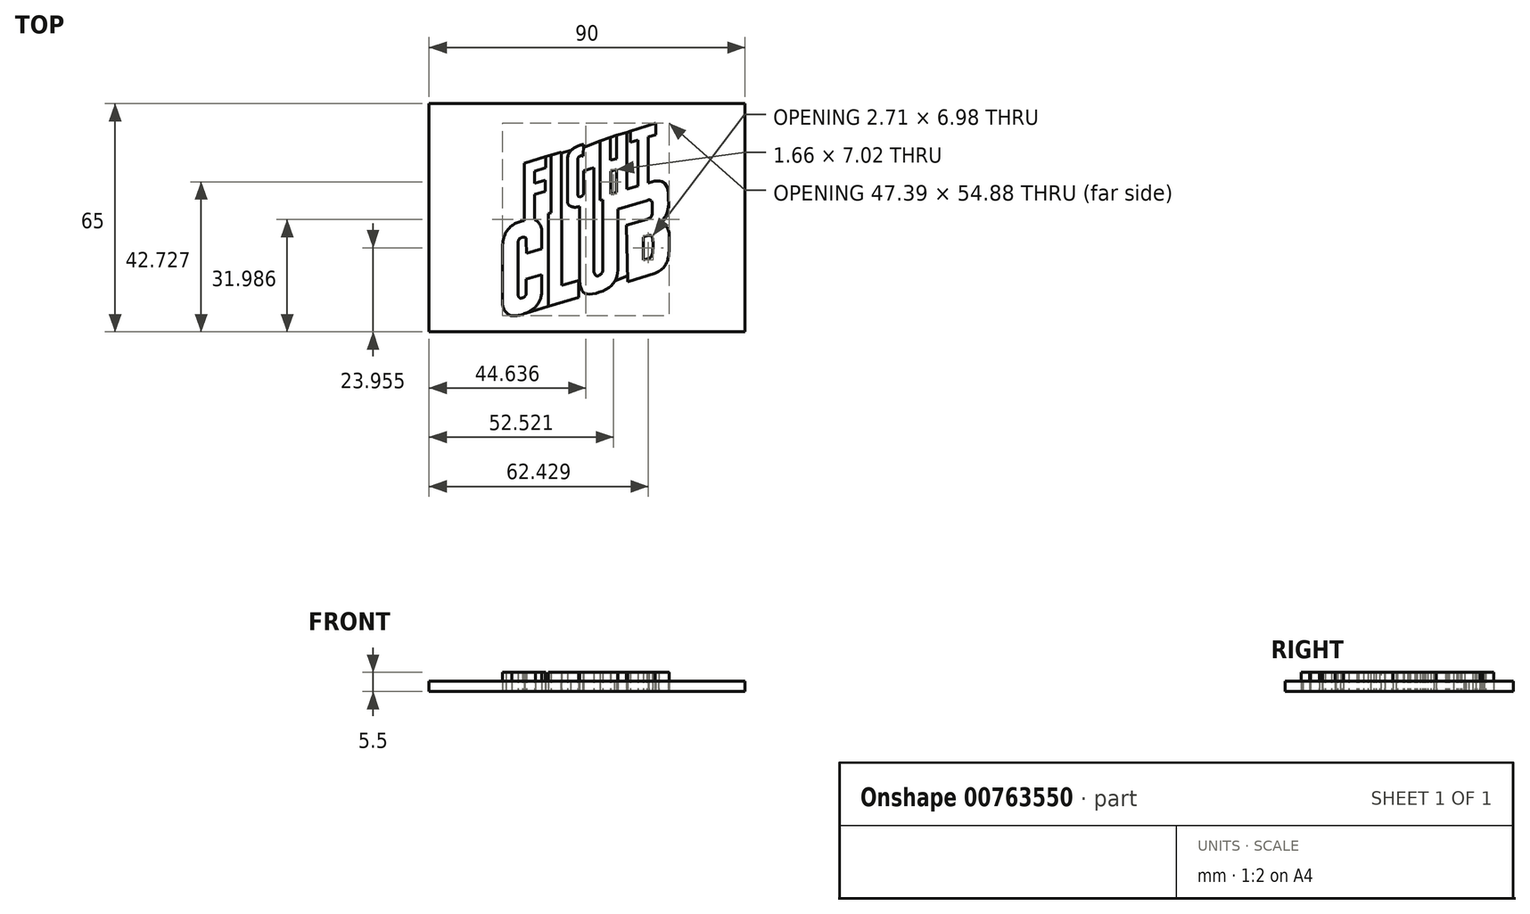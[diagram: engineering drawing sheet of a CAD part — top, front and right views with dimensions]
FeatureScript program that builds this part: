
annotation { "Feature Type Name" : "Feature", "Feature Type Description" : "" }
export const myFeature = defineFeature(function(context is Context, id is Id, definition is map)
    precondition{}
    {
        {
            var Q0;
            Q0=qCreatedBy(makeId("Top.planeOp"),FACE);
            var sketch = newSketch(context, id + "F0", { "sketchPlane" : qUnion([Q0])});
            skLineSegment(sketch, "E0", {"start": v(0, 29.17) * mm, "end": v(0, 40.63) * mm, "construction": true});
            skLineSegment(sketch, "E1", {"start": v(-11.79, 14.3) * mm, "end": v(-11.79, 17.39) * mm});
            skLineSegment(sketch, "E2", {"start": v(-11.79, 17.39) * mm, "end": v(-17.9, 15.52) * mm});
            skLineSegment(sketch, "E3", {"start": v(-17.9, 15.52) * mm, "end": v(-17.9, -0.84) * mm});
            skArc(sketch, "E4", {"start": v(-17.9, -0.84) * mm, "mid": v(-20.86, -1.84) * mm, "end": v(-23.05, -4.06) * mm});
            skArc(sketch, "E5", {"start": v(-23.05, -4.06) * mm, "mid": v(-23.84, -6) * mm, "end": v(-24.06, -8.1) * mm});
            skLineSegment(sketch, "E6", {"start": v(-24.06, -8.1) * mm, "end": v(-24.06, -24.5) * mm});
            skArc(sketch, "E7", {"start": v(-24.06, -24.5) * mm, "mid": v(-23.32, -26.69) * mm, "end": v(-21.4, -27.95) * mm});
            skArc(sketch, "E8", {"start": v(-21.4, -27.95) * mm, "mid": v(-17.85, -27.32) * mm, "end": v(-14.77, -25.45) * mm});
            skArc(sketch, "E9", {"start": v(-14.77, -25.45) * mm, "mid": v(-13.44, -23.46) * mm, "end": v(-12.97, -21.1) * mm});
            skLineSegment(sketch, "E10", {"start": v(-12.97, -21.1) * mm, "end": v(-12.9, -16.21) * mm});
            skLineSegment(sketch, "E11", {"start": v(-12.9, -16.21) * mm, "end": v(-17.32, -17.51) * mm});
            skLineSegment(sketch, "E12", {"start": v(-17.32, -17.51) * mm, "end": v(-17.32, -21.33) * mm});
            skArc(sketch, "E13", {"start": v(-18.38, -22.81) * mm, "mid": v(-17.61, -22.24) * mm, "end": v(-17.32, -21.33) * mm});
            skFitSpline(sketch, "E14", {"points": [v(-18.38, -22.81) * mm, v(-19.26, -22.81) * mm, v(-19.6, -22.2) * mm, v(-19.65, -21.74) * mm], "startDerivative": vector(-2.6, -0.52) * mm, "endDerivative": vector(-0.03, 1.52) * mm});
            skLineSegment(sketch, "E15", {"start": v(-19.65, -21.74) * mm, "end": v(-19.65, -7.2) * mm});
            skFitSpline(sketch, "E16", {"points": [v(-19.65, -7.2) * mm, v(-19.34, -6.08) * mm, v(-18.64, -5.6) * mm, v(-17.55, -5.65) * mm, v(-17.32, -6.58) * mm], "startDerivative": vector(0.18, 5.85) * mm, "endDerivative": vector(0, -4.67) * mm});
            skLineSegment(sketch, "E17", {"start": v(-17.32, -6.58) * mm, "end": v(-17.27, -10.17) * mm});
            skLineSegment(sketch, "E18", {"start": v(-17.27, -10.17) * mm, "end": v(-12.9, -8.8) * mm});
            skLineSegment(sketch, "E19", {"start": v(-12.9, -8.8) * mm, "end": v(-12.9, -4.15) * mm});
            skFitSpline(sketch, "E20", {"points": [v(-12.9, -4.15) * mm, v(-13.23, -2.36) * mm, v(-14.26, -0.9) * mm, v(-14.84, -0.62) * mm], "startDerivative": vector(-0.1, 5.35) * mm, "endDerivative": vector(-2.4, 0.79) * mm});
            skLineSegment(sketch, "E21", {"start": v(-14.84, -0.62) * mm, "end": v(-14.91, -0.62) * mm});
            skLineSegment(sketch, "E22", {"start": v(-14.91, -0.62) * mm, "end": v(-14.91, 6.66) * mm});
            skLineSegment(sketch, "E23", {"start": v(-14.91, 6.66) * mm, "end": v(-11.93, 7.57) * mm});
            skLineSegment(sketch, "E24", {"start": v(-11.93, 7.57) * mm, "end": v(-11.93, 10.68) * mm});
            skLineSegment(sketch, "E25", {"start": v(-11.93, 10.68) * mm, "end": v(-14.84, 9.85) * mm});
            skLineSegment(sketch, "E26", {"start": v(-14.84, 9.85) * mm, "end": v(-14.91, 9.82) * mm});
            skLineSegment(sketch, "E27", {"start": v(-14.91, 9.82) * mm, "end": v(-14.91, 13.28) * mm});
            skLineSegment(sketch, "E28", {"start": v(-14.91, 13.28) * mm, "end": v(-11.79, 14.3) * mm});
            skLineSegment(sketch, "E29", {"start": v(-7.35, 18.73) * mm, "end": v(-10.24, 17.82) * mm});
            skLineSegment(sketch, "E30", {"start": v(-10.24, 17.82) * mm, "end": v(-10.24, 1.4) * mm});
            skLineSegment(sketch, "E31", {"start": v(-10.24, 1.4) * mm, "end": v(-10.98, 1.14) * mm});
            skLineSegment(sketch, "E32", {"start": v(-10.98, 1.14) * mm, "end": v(-10.98, -25.2) * mm});
            skLineSegment(sketch, "E33", {"start": v(-10.98, -25.2) * mm, "end": v(-2.44, -22.65) * mm});
            skLineSegment(sketch, "E34", {"start": v(-2.44, -22.65) * mm, "end": v(-2.44, -17.83) * mm});
            skLineSegment(sketch, "E35", {"start": v(-2.44, -17.83) * mm, "end": v(-7.2, -19.25) * mm});
            skLineSegment(sketch, "E36", {"start": v(-7.2, -19.25) * mm, "end": v(-7.35, 18.73) * mm});
            skFitSpline(sketch, "E37", {"points": [v(-1.02, 20.93) * mm, v(-3.27, 20.17) * mm, v(-4.95, 18.7) * mm, v(-5.6, 16.65) * mm], "startDerivative": vector(-6.79, -1.77) * mm, "endDerivative": vector(-0.44, -7.25) * mm});
            skLineSegment(sketch, "E38", {"start": v(-5.6, 16.65) * mm, "end": v(-5.6, 4.51) * mm});
            skFitSpline(sketch, "E39", {"points": [v(-5.6, 4.51) * mm, v(-4.75, 3.3) * mm, v(-3.3, 3.02) * mm, v(-2.22, 3.16) * mm], "startDerivative": vector(0.44, -4.8) * mm, "endDerivative": vector(3.34, 0.64) * mm});
            skLineSegment(sketch, "E40", {"start": v(-2.22, 3.16) * mm, "end": v(-2.13, 3.16) * mm});
            skLineSegment(sketch, "E41", {"start": v(-2.13, 3.16) * mm, "end": v(-2.13, -18.02) * mm});
            skFitSpline(sketch, "E42", {"points": [v(-2.13, -18.02) * mm, v(-1.81, -19.83) * mm, v(-1.42, -20.7) * mm, v(-0.72, -21.43) * mm, v(0.48, -21.75) * mm, v(3.1, -21.35) * mm, v(5.96, -20.08) * mm, v(7.58, -18.53) * mm, v(8.4, -16.8) * mm, v(8.78, -14.72) * mm, v(8.81, -13.7) * mm], "startDerivative": vector(0.88, -18.82) * mm, "endDerivative": vector(0, 11.89) * mm});
            skLineSegment(sketch, "E43", {"start": v(8.81, -13.7) * mm, "end": v(8.81, 2.4) * mm});
            skLineSegment(sketch, "E44", {"start": v(8.81, 2.4) * mm, "end": v(17.06, 4.93) * mm});
            skFitSpline(sketch, "E45", {"points": [v(17.06, 4.93) * mm, v(17.61, 5.1) * mm, v(18.2, 4.93) * mm, v(18.53, 4.12) * mm, v(18.58, 3.23) * mm, v(18.52, 1.11) * mm, v(18.22, 0.23) * mm, v(17.68, -0.18) * mm, v(17.06, -0.42) * mm], "startDerivative": vector(5.26, 2.17) * mm, "endDerivative": vector(-5.78, -1.92) * mm});
            skLineSegment(sketch, "E46", {"start": v(17.06, -0.42) * mm, "end": v(11.24, -2.1) * mm});
            skLineSegment(sketch, "E47", {"start": v(11.24, -2.1) * mm, "end": v(11.52, -18.24) * mm});
            skLineSegment(sketch, "E48", {"start": v(11.52, -18.24) * mm, "end": v(19.26, -15.85) * mm});
            skFitSpline(sketch, "E49", {"points": [v(19.26, -15.85) * mm, v(20.2, -15.4) * mm, v(21.74, -14.25) * mm, v(22.83, -12.4) * mm, v(23.27, -10.48) * mm, v(23.33, -8.15) * mm], "startDerivative": vector(5.89, 2.48) * mm, "endDerivative": vector(0.02, 10.66) * mm});
            skFitSpline(sketch, "E50", {"points": [v(23.33, -8.15) * mm, v(23.33, -6.25) * mm, v(23.33, -5.01) * mm, v(23.33, -4.99) * mm, v(23.33, -4.12) * mm, v(22.64, -2.52) * mm, v(21.3, -1.73) * mm, v(20.42, -1.7) * mm, v(21.09, -1.18) * mm, v(21.98, -0.25) * mm, v(23.04, 2.14) * mm, v(23.2, 3.97) * mm, v(23.17, 6.68) * mm, v(23.13, 7.4) * mm, v(22.61, 9.27) * mm, v(21.4, 10.32) * mm, v(19.66, 10.5) * mm, v(17.56, 9.93) * mm], "startDerivative": vector(-0.03, 29.07) * mm, "endDerivative": vector(-29.21, -9.9) * mm});
            skLineSegment(sketch, "E51", {"start": v(17.56, 9.93) * mm, "end": v(17.44, 9.93) * mm});
            skLineSegment(sketch, "E52", {"start": v(17.44, 9.93) * mm, "end": v(17.44, 23.05) * mm});
            skLineSegment(sketch, "E53", {"start": v(17.44, 23.05) * mm, "end": v(19.62, 23.72) * mm});
            skLineSegment(sketch, "E54", {"start": v(19.62, 23.72) * mm, "end": v(19.62, 26.93) * mm});
            skLineSegment(sketch, "E55", {"start": v(19.62, 26.93) * mm, "end": v(12.3, 24.63) * mm});
            skLineSegment(sketch, "E56", {"start": v(12.3, 24.63) * mm, "end": v(12.3, 21.56) * mm});
            skLineSegment(sketch, "E57", {"start": v(12.3, 21.56) * mm, "end": v(14.5, 22.17) * mm});
            skLineSegment(sketch, "E58", {"start": v(14.5, 22.17) * mm, "end": v(14.5, 9.05) * mm});
            skLineSegment(sketch, "E59", {"start": v(14.5, 9.05) * mm, "end": v(11.35, 8.14) * mm});
            skLineSegment(sketch, "E60", {"start": v(11.35, 8.14) * mm, "end": v(11.35, 24.33) * mm});
            skLineSegment(sketch, "E61", {"start": v(11.35, 24.33) * mm, "end": v(8.42, 23.49) * mm});
            skLineSegment(sketch, "E62", {"start": v(8.42, 23.49) * mm, "end": v(8.42, 16.84) * mm});
            skLineSegment(sketch, "E63", {"start": v(8.42, 16.84) * mm, "end": v(6.67, 16.37) * mm});
            skLineSegment(sketch, "E64", {"start": v(6.67, 16.37) * mm, "end": v(6.67, 22.88) * mm});
            skLineSegment(sketch, "E65", {"start": v(6.67, 22.88) * mm, "end": v(3.73, 21.86) * mm});
            skLineSegment(sketch, "E66", {"start": v(3.73, 21.86) * mm, "end": v(3.73, 4.97) * mm});
            skLineSegment(sketch, "E67", {"start": v(3.73, 4.97) * mm, "end": v(4.46, 5.13) * mm});
            skLineSegment(sketch, "E68", {"start": v(4.46, 5.13) * mm, "end": v(4.46, -14.27) * mm});
            skFitSpline(sketch, "E69", {"points": [v(4.46, -14.27) * mm, v(4.46, -15.18) * mm, v(3.72, -16.26) * mm, v(2.72, -16.55) * mm, v(2.06, -15.8) * mm, v(1.94, -14.27) * mm], "startDerivative": vector(0, -3.25) * mm, "endDerivative": vector(-0.37, 7.2) * mm});
            skLineSegment(sketch, "E70", {"start": v(1.94, -14.27) * mm, "end": v(1.94, 14.26) * mm});
            skLineSegment(sketch, "E71", {"start": v(1.94, 14.26) * mm, "end": v(-0.98, 13.41) * mm});
            skPoint(sketch, "E71.endSnap0", {"position": v(3.73, 13.41) * mm});
            skLineSegment(sketch, "E72", {"start": v(-0.98, 13.41) * mm, "end": v(-0.98, 7.4) * mm});
            skFitSpline(sketch, "E73", {"points": [v(-0.98, 7.4) * mm, v(-0.98, 7.13) * mm, v(-1.1, 6.59) * mm, v(-1.46, 6.16) * mm, v(-2.38, 6) * mm, v(-2.65, 6.68) * mm], "startDerivative": vector(-0.05, -1.86) * mm, "endDerivative": vector(0.17, 3.62) * mm});
            skLineSegment(sketch, "E74", {"start": v(-2.65, 6.68) * mm, "end": v(-2.65, 16.65) * mm});
            skArc(sketch, "E75", {"start": v(-1.57, 17.66) * mm, "mid": v(-2.33, 17.39) * mm, "end": v(-2.65, 16.65) * mm});
            skArc(sketch, "E76", {"start": v(-1.18, 17.52) * mm, "mid": v(-1.37, 17.62) * mm, "end": v(-1.57, 17.66) * mm});
            skLineSegment(sketch, "E77", {"start": v(-1.18, 17.52) * mm, "end": v(-1.02, 20.93) * mm});
            skLineSegment(sketch, "E78", {"start": v(6.69, 13.22) * mm, "end": v(6.69, 6.72) * mm});
            skLineSegment(sketch, "E79", {"start": v(6.69, 6.72) * mm, "end": v(8.35, 7.26) * mm});
            skLineSegment(sketch, "E80", {"start": v(8.35, 7.26) * mm, "end": v(8.35, 13.74) * mm});
            skLineSegment(sketch, "E81", {"start": v(8.35, 13.74) * mm, "end": v(6.69, 13.22) * mm});
            skLineSegment(sketch, "E82", {"start": v(16.08, -5.5) * mm, "end": v(16.08, -12.04) * mm});
            skLineSegment(sketch, "E83", {"start": v(16.08, -12.04) * mm, "end": v(17.68, -11.53) * mm});
            skFitSpline(sketch, "E84", {"points": [v(17.68, -11.53) * mm, v(18.26, -11.11) * mm, v(18.66, -9.8) * mm, v(18.78, -7.26) * mm, v(18.46, -5.26) * mm, v(17.88, -5) * mm, v(16.08, -5.5) * mm], "startDerivative": vector(5.42, 2.74) * mm, "endDerivative": vector(-10.7, -3.8) * mm});
            skPoint(sketch, "E85.middle", {"position": v(0, 0) * mm});
            skPoint(sketch, "E86.start.orphan", {"position": v(-26.8, 29.76) * mm});
            skPoint(sketch, "E87.start.orphan", {"position": v(26.8, 29.76) * mm});
            skPoint(sketch, "E88.top.end.orphan", {"position": v(-26.8, -29.76) * mm});
            skPoint(sketch, "E88.top.start.orphan", {"position": v(26.8, -29.76) * mm});
            skPoint(sketch, "E89.bottom.start.orphan", {"position": v(-23.32, -26.69) * mm});
            skLineSegment(sketch, "E90.bottom", {"start": v(45, 32.5) * mm, "end": v(-45, 32.5) * mm});
            skLineSegment(sketch, "E90.top", {"start": v(45, -32.5) * mm, "end": v(-45, -32.5) * mm});
            skLineSegment(sketch, "E90.left", {"start": v(45, 32.5) * mm, "end": v(45, -32.5) * mm});
            skLineSegment(sketch, "E90.right", {"start": v(-45, 32.5) * mm, "end": v(-45, -32.5) * mm});
            skSolve(sketch);
        }
        {
            var Q0;
            Q0=makeQuery(id+"F0.imprint","IMPRINT",FACE,{"disambiguationData":[TD([[makeQuery(id+"F0.imprint","IMPRINT",EDGE,{"derivedFrom":sQuery(id+"F0.wireOp",EDGE,"E1")}),-1.0]])]});
            extrude(context, id + "F1", {"entities" : qUnion([Q0]), "depth" : 3 * mm, "offsetDistance" : 25 * mm});
        }
        {
            var Q0;
            Q0=makeQuery(id+"F0.imprint","IMPRINT",FACE,{"disambiguationData":[TD([[makeQuery(id+"F0.imprint","IMPRINT",EDGE,{"derivedFrom":sQuery(id+"F0.wireOp",EDGE,"E1")}),1.0]])]});
            var Q1;
            Q1=makeQuery(id+"F0.imprint","IMPRINT",FACE,{"disambiguationData":[TD([[makeQuery(id+"F0.imprint","IMPRINT",EDGE,{"derivedFrom":sQuery(id+"F0.wireOp",EDGE,"E29")}),1.0]])]});
            var Q2;
            Q2=makeQuery(id+"F0.imprint","IMPRINT",FACE,{"disambiguationData":[TD([[makeQuery(id+"F0.imprint","IMPRINT",EDGE,{"derivedFrom":sQuery(id+"F0.wireOp",EDGE,"E37")}),1.0]])]});
            extrude(context, id + "F2", {"entities" : qUnion([Q0, Q1, Q2]), "depth" : 5.5 * mm, "offsetDistance" : 25 * mm});
        }
        {
            var Q0;
            Q0=makeQuery(id+"F1.opExtrude","CAP_FACE",FACE,{"disambiguationData":[OSD([sQuery(id+"F0.wireOp",EDGE,"E1"),sQuery(id+"F0.wireOp",EDGE,"E2"),sQuery(id+"F0.wireOp",EDGE,"E3"),sQuery(id+"F0.wireOp",EDGE,"E4"),sQuery(id+"F0.wireOp",EDGE,"E5"),sQuery(id+"F0.wireOp",EDGE,"E6"),sQuery(id+"F0.wireOp",EDGE,"E7"),sQuery(id+"F0.wireOp",EDGE,"E8"),sQuery(id+"F0.wireOp",EDGE,"E9"),sQuery(id+"F0.wireOp",EDGE,"E10"),sQuery(id+"F0.wireOp",EDGE,"E11"),sQuery(id+"F0.wireOp",EDGE,"E12"),sQuery(id+"F0.wireOp",EDGE,"E13"),sQuery(id+"F0.wireOp",EDGE,"E14"),sQuery(id+"F0.wireOp",EDGE,"E15"),sQuery(id+"F0.wireOp",EDGE,"E16"),sQuery(id+"F0.wireOp",EDGE,"E17"),sQuery(id+"F0.wireOp",EDGE,"E18"),sQuery(id+"F0.wireOp",EDGE,"E19"),sQuery(id+"F0.wireOp",EDGE,"E20"),sQuery(id+"F0.wireOp",EDGE,"E21"),sQuery(id+"F0.wireOp",EDGE,"E22"),sQuery(id+"F0.wireOp",EDGE,"E23"),sQuery(id+"F0.wireOp",EDGE,"E24"),sQuery(id+"F0.wireOp",EDGE,"E25"),sQuery(id+"F0.wireOp",EDGE,"E26"),sQuery(id+"F0.wireOp",EDGE,"E27"),sQuery(id+"F0.wireOp",EDGE,"E28"),sQuery(id+"F0.wireOp",EDGE,"E29"),sQuery(id+"F0.wireOp",EDGE,"E30"),sQuery(id+"F0.wireOp",EDGE,"E31"),sQuery(id+"F0.wireOp",EDGE,"E32"),sQuery(id+"F0.wireOp",EDGE,"E33"),sQuery(id+"F0.wireOp",EDGE,"E34"),sQuery(id+"F0.wireOp",EDGE,"E35"),sQuery(id+"F0.wireOp",EDGE,"E36"),sQuery(id+"F0.wireOp",EDGE,"E37"),sQuery(id+"F0.wireOp",EDGE,"E38"),sQuery(id+"F0.wireOp",EDGE,"E39"),sQuery(id+"F0.wireOp",EDGE,"E40"),sQuery(id+"F0.wireOp",EDGE,"E41"),sQuery(id+"F0.wireOp",EDGE,"E42"),sQuery(id+"F0.wireOp",EDGE,"E43"),sQuery(id+"F0.wireOp",EDGE,"E44"),sQuery(id+"F0.wireOp",EDGE,"E45"),sQuery(id+"F0.wireOp",EDGE,"E46"),sQuery(id+"F0.wireOp",EDGE,"E47"),sQuery(id+"F0.wireOp",EDGE,"E48"),sQuery(id+"F0.wireOp",EDGE,"E49"),sQuery(id+"F0.wireOp",EDGE,"E50"),sQuery(id+"F0.wireOp",EDGE,"E51"),sQuery(id+"F0.wireOp",EDGE,"E52"),sQuery(id+"F0.wireOp",EDGE,"E53"),sQuery(id+"F0.wireOp",EDGE,"E55"),sQuery(id+"F0.wireOp",EDGE,"E56"),sQuery(id+"F0.wireOp",EDGE,"E57"),sQuery(id+"F0.wireOp",EDGE,"E58"),sQuery(id+"F0.wireOp",EDGE,"E59"),sQuery(id+"F0.wireOp",EDGE,"E60"),sQuery(id+"F0.wireOp",EDGE,"E61"),sQuery(id+"F0.wireOp",EDGE,"E62"),sQuery(id+"F0.wireOp",EDGE,"E63"),sQuery(id+"F0.wireOp",EDGE,"E64"),sQuery(id+"F0.wireOp",EDGE,"E65"),sQuery(id+"F0.wireOp",EDGE,"E66"),sQuery(id+"F0.wireOp",EDGE,"E67"),sQuery(id+"F0.wireOp",EDGE,"E68"),sQuery(id+"F0.wireOp",EDGE,"E69"),sQuery(id+"F0.wireOp",EDGE,"E70"),sQuery(id+"F0.wireOp",EDGE,"E71"),sQuery(id+"F0.wireOp",EDGE,"E72"),sQuery(id+"F0.wireOp",EDGE,"E73"),sQuery(id+"F0.wireOp",EDGE,"E74"),sQuery(id+"F0.wireOp",EDGE,"E75"),sQuery(id+"F0.wireOp",EDGE,"E76"),sQuery(id+"F0.wireOp",EDGE,"E77"),sQuery(id+"F0.wireOp",EDGE,"E54"),sQuery(id+"F0.wireOp",EDGE,"E90.bottom"),sQuery(id+"F0.wireOp",EDGE,"E90.top"),sQuery(id+"F0.wireOp",EDGE,"E90.left"),sQuery(id+"F0.wireOp",EDGE,"E90.right")])],"isStart":false});
            var sketch = newSketch(context, id + "F3", { "sketchPlane" : qUnion([Q0])});
            skPoint(sketch, "E91.startSnap0", {"position": v(-17.61, -22.24) * mm});
            skPoint(sketch, "E91.start.orphan", {"position": v(-17.61, -27.23) * mm});
            skLineSegment(sketch, "E92", {"start": v(-17.61, -27.23) * mm, "end": v(-10.98, -25.2) * mm});
            skLineSegment(sketch, "E93", {"start": v(-2.44, -22.65) * mm, "end": v(0.82, -21.75) * mm});
            skLineSegment(sketch, "E94", {"start": v(-11.79, 17.39) * mm, "end": v(-7.35, 18.73) * mm});
            skLineSegment(sketch, "E95", {"start": v(11.35, 24.33) * mm, "end": v(12.3, 24.63) * mm});
            skLineSegment(sketch, "E96", {"start": v(6.67, 22.88) * mm, "end": v(8.42, 23.49) * mm});
            skLineSegment(sketch, "E97", {"start": v(-2.44, -17.83) * mm, "end": v(-2.13, -17.83) * mm});
            skLineSegment(sketch, "E98", {"start": v(-7.35, 18.52) * mm, "end": v(-4.55, 19.2) * mm});
            skLineSegment(sketch, "E99", {"start": v(-1.07, 19.97) * mm, "end": v(3.73, 21.86) * mm});
            skLineSegment(sketch, "E100", {"start": v(7.95, -17.94) * mm, "end": v(11.49, -16.58) * mm});
            skSolve(sketch);
        }
        {
            var Q0;
            {var subQ1=sQuery(id+"F3.wireOp",EDGE,"E92");Q0=makeQuery(id+"F3.imprint","IMPRINT",FACE,{"disambiguationData":[TD([[makeQuery(id+"F3.imprint","IMPRINT",EDGE,{"derivedFrom":subQ1}),1.0]])]});}
            var Q1;
            Q1=makeQuery(id+"F3.imprint","IMPRINT",FACE,{"disambiguationData":[TD([[makeQuery(id+"F3.imprint","IMPRINT",EDGE,{"derivedFrom":sQuery(id+"F3.wireOp",EDGE,"3dhdLZRf-anwa-GZ4C-T9eZ-SivqKJuPEOgX")}),-1.0]])]});
            var Q2;
            {var subQ1=sQuery(id+"F3.wireOp",EDGE,"BJmdIdnz-Clv5-6TnT-cXyy-2DFI0YhgusDD");Q2=makeQuery(id+"F3.imprint","IMPRINT",FACE,{"disambiguationData":[TD([[makeQuery(id+"F3.imprint","IMPRINT",EDGE,{"derivedFrom":subQ1}),-1.0]])]});}
            var Q3;
            Q3=makeQuery(id+"F3.imprint","IMPRINT",FACE,{"disambiguationData":[TD([[makeQuery(id+"F3.imprint","IMPRINT",EDGE,{"derivedFrom":sQuery(id+"F3.wireOp",EDGE,"E95")}),-1.0]])]});
            var Q4;
            Q4=makeQuery(id+"F3.imprint","IMPRINT",FACE,{"disambiguationData":[TD([[makeQuery(id+"F3.imprint","IMPRINT",EDGE,{"derivedFrom":sQuery(id+"F3.wireOp",EDGE,"E96")}),-1.0]])]});
            var Q5;
            {var subQ3=sQuery(id+"F3.wireOp",EDGE,"E97");Q5=makeQuery(id+"F3.imprint","IMPRINT",FACE,{"disambiguationData":[TD([[makeQuery(id+"F3.imprint","IMPRINT",EDGE,{"derivedFrom":subQ3}),1.0]])]});}
            var Q6;
            {var subQ2=sQuery(id+"F3.wireOp",EDGE,"E99");Q6=makeQuery(id+"F3.imprint","IMPRINT",FACE,{"disambiguationData":[TD([[makeQuery(id+"F3.imprint","IMPRINT",EDGE,{"derivedFrom":subQ2}),-1.0]])]});}
            var Q7;
            {var subQ2=sQuery(id+"F3.wireOp",EDGE,"E100");Q7=makeQuery(id+"F3.imprint","IMPRINT",FACE,{"disambiguationData":[TD([[makeQuery(id+"F3.imprint","IMPRINT",EDGE,{"derivedFrom":subQ2}),1.0]])]});}
            extrude(context, id + "F4", {"entities" : qUnion([Q0, Q1, Q2, Q3, Q4, Q5, Q6, Q7]), "operationType" : NewBodyOperationType.REMOVE, "oppositeDirection" : true, "depth" : 25 * mm, "offsetDistance" : 25 * mm});
        }
    });
